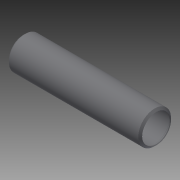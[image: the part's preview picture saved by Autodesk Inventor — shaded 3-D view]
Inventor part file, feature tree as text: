
AUTODESK INVENTOR PART (.ipt)
format: ipt  version: 2014 (Build 180170000, 170)  size: 127,488 bytes
history: native  units: in
note: dims shown in document units (in); Inventor stores cm internally (conversion verified against a paired STEP export)
features: other x56, revolve x1, sketch x1
ambient origin geometry x8: Origin, YZ Plane, XZ Plane, XY Plane, X Axis, Y Axis, Z Axis, Center Point
bodies: Solid1 (feature_tree)
feature tree (58):
  revolve  "Revolution1"  [1 undecoded]
  other  "o1_XY"
  other  "o1_YZ"
  other  "o1_ZX"
  other  "o1_X"
  other  "o1_Y"
  other  "o1_Z"
  other  "o1_Center"
  other  "o2_XY"
  other  "o2_YZ"
  other  "o2_ZX"
  other  "o2_X"
  other  "o2_Y"
  other  "o2_Z"
  other  "o2_Center"
  other  "t1_XY"
  other  "t1_YZ"
  other  "t1_ZX"
  other  "t1_X"
  other  "t1_Y"
  other  "t1_Z"
  other  "t1_Center"
  other  "t2_XY"
  other  "t2_YZ"
  other  "t2_ZX"
  other  "t2_X"
  other  "t2_Y"
  other  "t2_Z"
  other  "t2_Center"
  other  "t3_XY"
  other  "t3_YZ"
  other  "t3_ZX"
  other  "t3_X"
  other  "t3_Y"
  other  "t3_Z"
  other  "t3_Center"
  other  "t4_XY"
  other  "t4_YZ"
  other  "t4_ZX"
  other  "t4_X"
  other  "t4_Y"
  other  "t4_Z"
  other  "t4_Center"
  other  "tube1_XY"
  other  "tube1_YZ"
  other  "tube1_ZX"
  other  "tube1_X"
  other  "tube1_Y"
  other  "tube1_Z"
  other  "tube1_Center"
  other  "tube2_XY"
  other  "tube2_YZ"
  other  "tube2_ZX"
  other  "tube2_X"
  other  "tube2_Y"
  other  "tube2_Z"
  other  "tube2_Center"
  sketch  "Sketch_5"  dims[d0=360.0deg]
note: 1 required parameter value undecoded (feature->parameter linkage not recoverable at this tier; creation-order binding heuristic only, values carry confidence <= 0.55)
